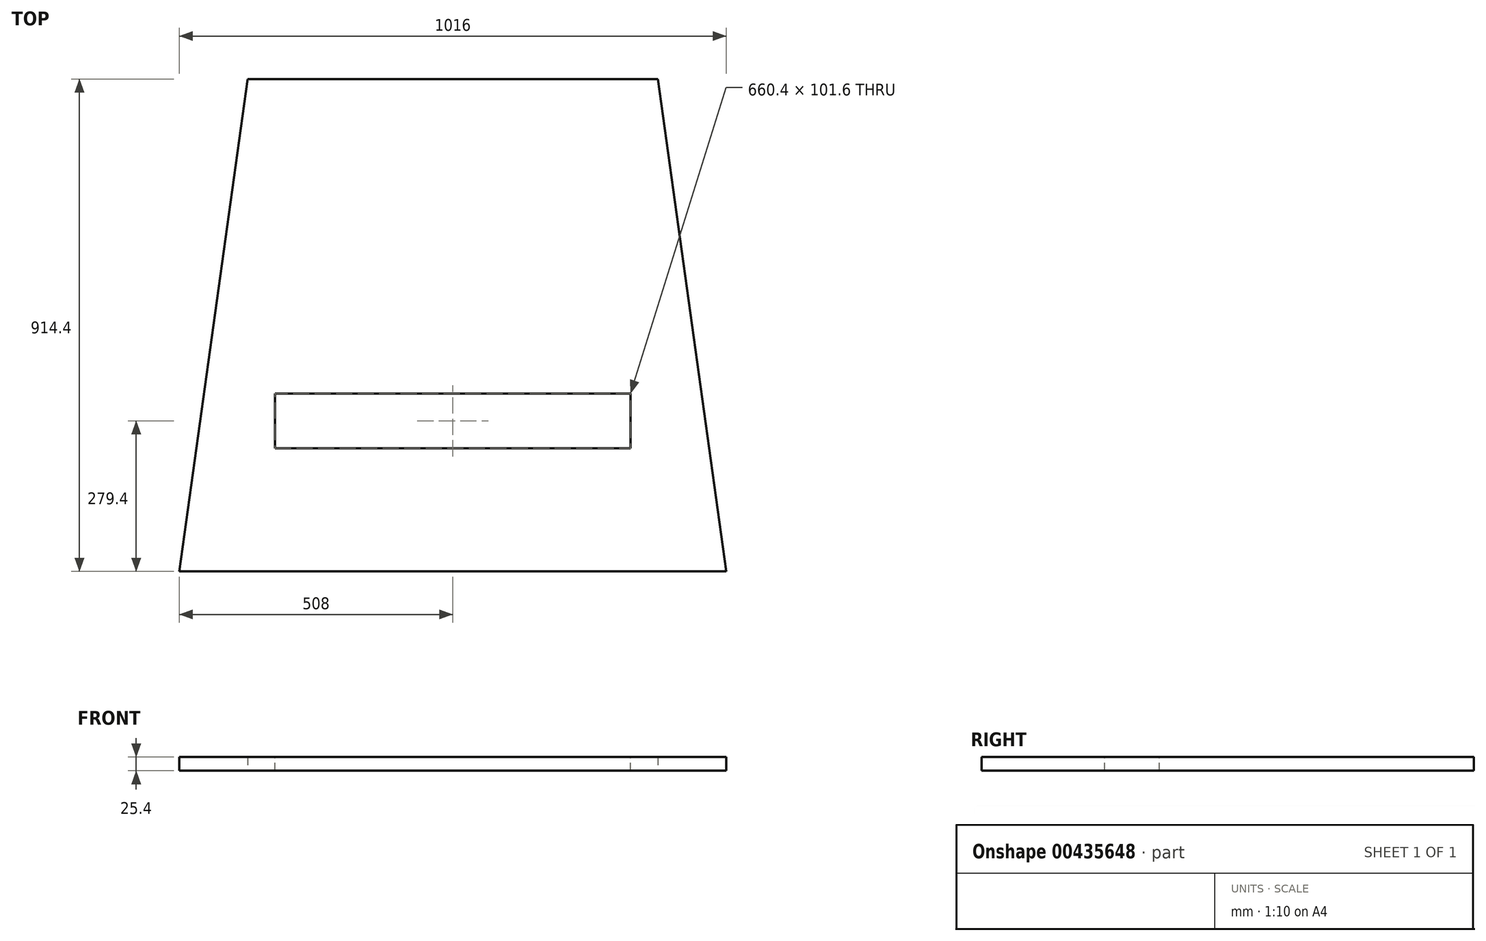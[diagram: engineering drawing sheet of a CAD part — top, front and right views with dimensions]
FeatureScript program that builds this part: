
annotation { "Feature Type Name" : "Feature", "Feature Type Description" : "" }
export const myFeature = defineFeature(function(context is Context, id is Id, definition is map)
    precondition{}
    {
        {
            var Q0;
            Q0=qCreatedBy(makeId("Top.planeOp"),FACE);
            var sketch = newSketch(context, id + "F0", { "sketchPlane" : qUnion([Q0])});
            skLineSegment(sketch, "E0.bottom", {"start": v(508, -457.2) * mm, "end": v(-508, -457.2) * mm});
            skLineSegment(sketch, "E0.top", {"start": v(508, 457.2) * mm, "end": v(-508, 457.2) * mm});
            skLineSegment(sketch, "E0.left", {"start": v(508, -457.2) * mm, "end": v(508, 457.2) * mm});
            skLineSegment(sketch, "E0.right", {"start": v(-508, -457.2) * mm, "end": v(-508, 457.2) * mm});
            skPoint(sketch, "E0.middle", {"position": v(0, 0) * mm});
            skPoint(sketch, "E1", {"position": v(-381, 457.2) * mm});
            skPoint(sketch, "E2", {"position": v(0, 457.2) * mm});
            skPoint(sketch, "E3", {"position": v(381, 457.2) * mm});
            skLineSegment(sketch, "E4", {"start": v(-381, 457.2) * mm, "end": v(-508, -457.2) * mm});
            skLineSegment(sketch, "E5", {"start": v(381, 457.2) * mm, "end": v(508, -457.2) * mm});
            skSolve(sketch);
        }
        {
            var Q0;
            Q0=makeQuery(id+"F0.imprint","IMPRINT",FACE,{"disambiguationData":[TD([[makeQuery(id+"F0.imprint","IMPRINT",EDGE,{"derivedFrom":sQuery(id+"F0.wireOp",EDGE,"E0.bottom")}),-1.0]])]});
            extrude(context, id + "F1", {"entities" : qUnion([Q0]), "depth" : 25.4 * mm});
        }
        {
            var Q0;
            Q0=makeQuery(id+"F1.opExtrude","CAP_FACE",FACE,{"disambiguationData":[OSD([sQuery(id+"F0.wireOp",EDGE,"E0.bottom"),sQuery(id+"F0.wireOp",EDGE,"E0.top"),sQuery(id+"F0.wireOp",EDGE,"E4"),sQuery(id+"F0.wireOp",EDGE,"E5")])],"isStart":false});
            var sketch = newSketch(context, id + "F2", { "sketchPlane" : qUnion([Q0])});
            skLineSegment(sketch, "E6.bottom", {"start": v(330.2, -228.6) * mm, "end": v(-330.2, -228.6) * mm});
            skLineSegment(sketch, "E6.top", {"start": v(330.2, -127) * mm, "end": v(-330.2, -127) * mm});
            skLineSegment(sketch, "E6.left", {"start": v(330.2, -228.6) * mm, "end": v(330.2, -127) * mm});
            skLineSegment(sketch, "E6.right", {"start": v(-330.2, -228.6) * mm, "end": v(-330.2, -127) * mm});
            skPoint(sketch, "E6.middle", {"position": v(0, -177.8) * mm});
            skSolve(sketch);
        }
        {
            var Q0;
            Q0=makeQuery(id+"F2.imprint","IMPRINT",FACE,{"disambiguationData":[TD([[makeQuery(id+"F2.imprint","IMPRINT",EDGE,{"derivedFrom":sQuery(id+"F2.wireOp",EDGE,"E6.bottom")}),-1.0]])]});
            extrude(context, id + "F3", {"entities" : qUnion([Q0]), "operationType" : NewBodyOperationType.REMOVE, "oppositeDirection" : true, "depth" : 25.4 * mm});
        }
    });
